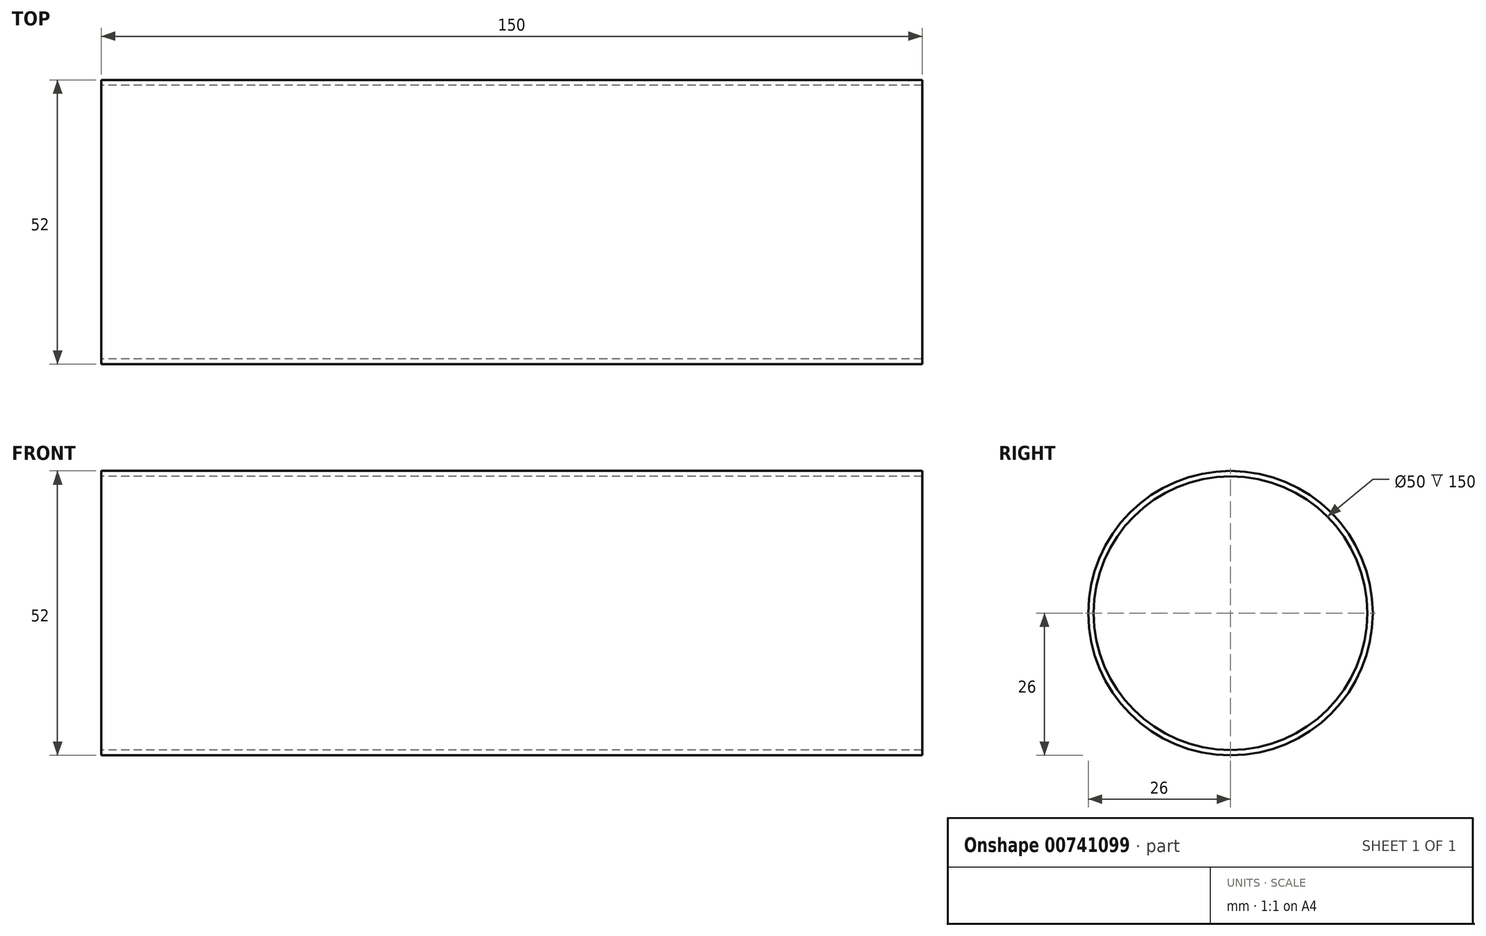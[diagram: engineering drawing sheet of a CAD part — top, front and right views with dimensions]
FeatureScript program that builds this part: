
annotation { "Feature Type Name" : "Feature", "Feature Type Description" : "" }
export const myFeature = defineFeature(function(context is Context, id is Id, definition is map)
    precondition{}
    {
        {
            var Q0;
            Q0=qCreatedBy(makeId("Right.planeOp"),FACE);
            var sketch = newSketch(context, id + "F0", { "sketchPlane" : qUnion([Q0])});
            skCircle(sketch, "E0", {"center": v(0, 0) * mm, "radius": 26 * mm});
            skCircle(sketch, "E1", {"center": v(0, 0) * mm, "radius": 25 * mm});
            skSolve(sketch);
        }
        {
            var Q0;
            Q0=qSketchRegion(id+"F0",true);
            extrude(context, id + "F1", {"entities" : qUnion([Q0]), "endBound" : BoundingType.SYMMETRIC, "depth" : 150 * mm, "offsetDistance" : 25 * mm});
        }
    });
